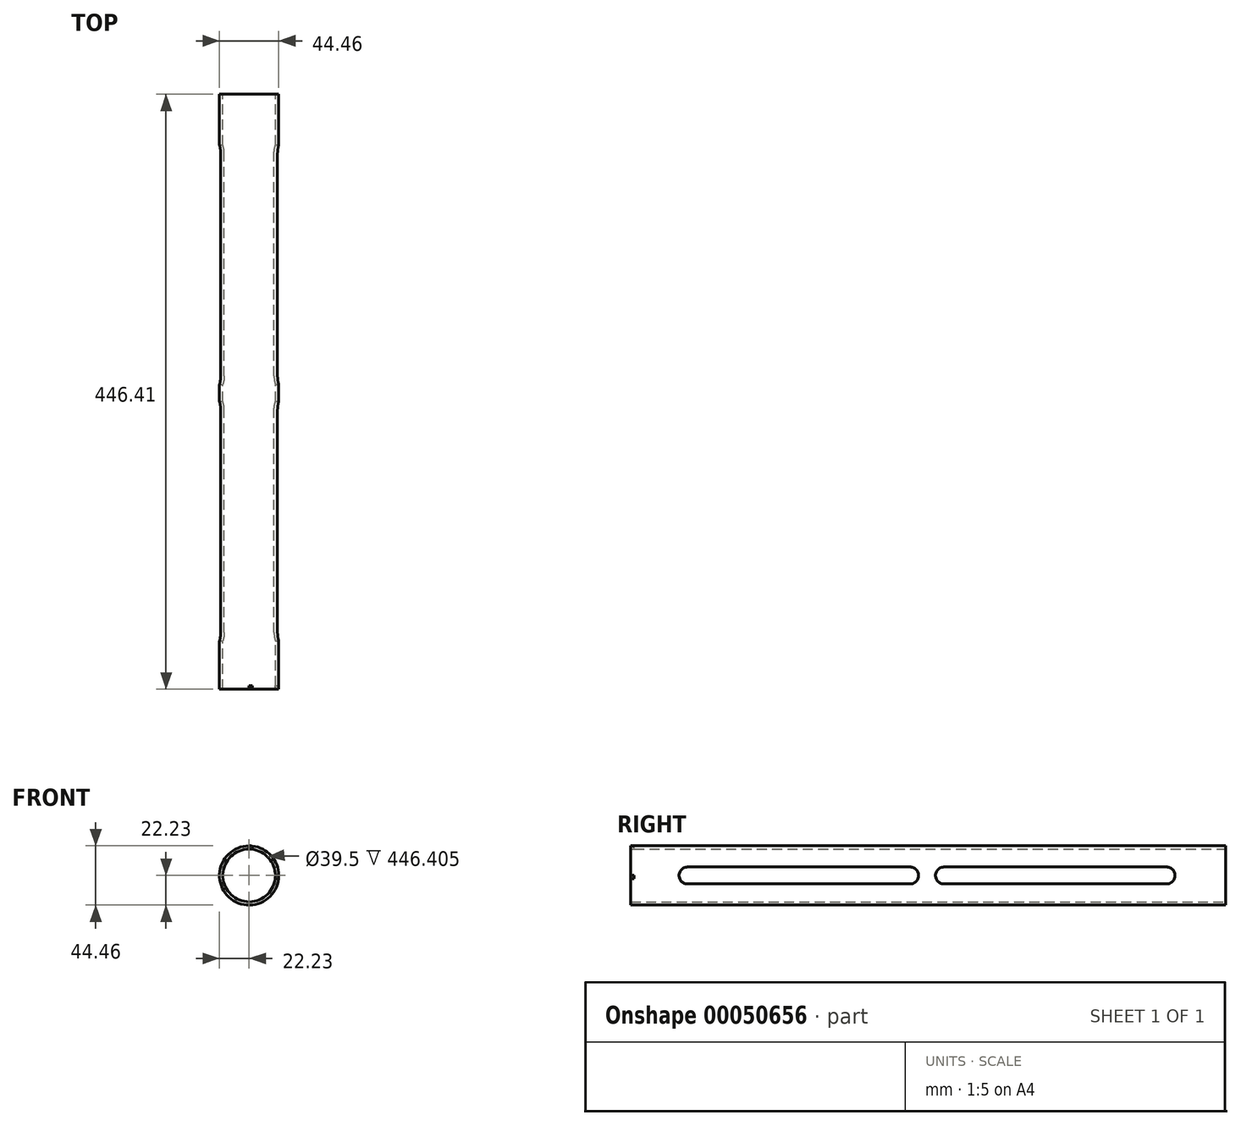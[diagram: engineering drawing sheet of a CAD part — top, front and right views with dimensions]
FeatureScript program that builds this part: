
annotation { "Feature Type Name" : "Feature", "Feature Type Description" : "" }
export const myFeature = defineFeature(function(context is Context, id is Id, definition is map)
    precondition{}
    {
        {
            var Q0;
            Q0=qCreatedBy(makeId("Front.planeOp"),FACE);
            var sketch = newSketch(context, id + "F0", { "sketchPlane" : qUnion([Q0])});
            skCircle(sketch, "E0", {"center": v(0, 0) * mm, "radius": 22.23 * mm});
            skCircle(sketch, "E1", {"center": v(0, 0) * mm, "radius": 19.75 * mm});
            skSolve(sketch);
        }
        {
            var Q0;
            Q0 = qSketchRegion(id + "F0", true);
            extrude(context, id + "F1", {"entities" : qUnion([Q0]), "depth" : 446.4 * mm});
        }
        {
            var Q0;
            Q0=qCreatedBy(makeId("Right.planeOp"),FACE);
            var sketch = newSketch(context, id + "F2", { "sketchPlane" : qUnion([Q0])});
            skLineSegment(sketch, "E2.bottom", {"start": v(-38.1, 0) * mm, "end": v(-155.7, 0) * mm});
            skLineSegment(sketch, "E2.top", {"start": v(-44.45, 6.35) * mm, "end": v(-211.46, 6.35) * mm});
            skLineSegment(sketch, "E2.left", {"start": v(-38.1, 0) * mm, "end": v(-38.1, 0) * mm});
            skPoint(sketch, "E3.visualSharp", {"position": v(-152.9, 6.35) * mm});
            skArc(sketch, "E3.filletArc", {"start": v(-211.46, 6.35) * mm, "mid": v(-215.95, 4.5) * mm, "end": v(-217.8, 0) * mm});
            skPoint(sketch, "E4.visualSharp", {"position": v(-38.1, 6.35) * mm});
            skArc(sketch, "E4.filletArc", {"start": v(-38.1, 0) * mm, "mid": v(-39.96, 4.5) * mm, "end": v(-44.45, 6.35) * mm});
            skArc(sketch, "E5.MirrorCS", {"start": v(-211.46, -6.35) * mm, "mid": v(-215.95, -4.5) * mm, "end": v(-217.8, 0) * mm});
            skPoint(sketch, "E6.MirrorP", {"position": v(-38.1, -6.35) * mm});
            skLineSegment(sketch, "E7.MirrorCS", {"start": v(-44.45, -6.35) * mm, "end": v(-211.46, -6.35) * mm});
            skArc(sketch, "E8.MirrorCS", {"start": v(-38.1, 0) * mm, "mid": v(-39.96, -4.5) * mm, "end": v(-44.45, -6.35) * mm});
            skPoint(sketch, "E9.MirrorP", {"position": v(-152.9, -6.35) * mm});
            skLineSegment(sketch, "E10", {"start": v(-224.16, 31.09) * mm, "end": v(-224.16, -31.58) * mm, "construction": true});
            skLineSegment(sketch, "E11.MirrorCS", {"start": v(-410.21, 0) * mm, "end": v(-410.21, 0) * mm});
            skLineSegment(sketch, "E12.MirrorCS", {"start": v(-403.86, 6.35) * mm, "end": v(-236.86, 6.35) * mm});
            skLineSegment(sketch, "E13.MirrorCS", {"start": v(-403.86, -6.35) * mm, "end": v(-236.86, -6.35) * mm});
            skArc(sketch, "E14.MirrorCS", {"start": v(-236.86, -6.35) * mm, "mid": v(-232.36, -4.5) * mm, "end": v(-230.5, 0) * mm});
            skArc(sketch, "E15.MirrorCS", {"start": v(-410.21, 0) * mm, "mid": v(-408.35, 4.5) * mm, "end": v(-403.86, 6.35) * mm});
            skArc(sketch, "E16.MirrorCS", {"start": v(-236.86, 6.35) * mm, "mid": v(-232.36, 4.5) * mm, "end": v(-230.5, 0) * mm});
            skPoint(sketch, "E17.MirrorP", {"position": v(-410.21, 6.35) * mm});
            skPoint(sketch, "E18.MirrorP", {"position": v(-410.21, -6.35) * mm});
            skArc(sketch, "E19.MirrorCS", {"start": v(-410.21, 0) * mm, "mid": v(-408.35, -4.5) * mm, "end": v(-403.86, -6.35) * mm});
            skSolve(sketch);
        }
        {
            var Q0;
            Q0 = qSketchRegion(id + "F2", true);
            extrude(context, id + "F3", {"entities" : qUnion([Q0]), "operationType" : NewBodyOperationType.REMOVE, "endBound" : BoundingType.SYMMETRIC, "oppositeDirection" : true, "depth" : 127 * mm});
        }
        {
            var Q0;
            Q0=makeQuery(id+"F1.opExtrude","CAP_FACE",FACE,{"disambiguationData":[OSD([sQuery(id+"F0.wireOp",EDGE,"E0"),sQuery(id+"F0.wireOp",EDGE,"E1")])],"isStart":false});
            var sketch = newSketch(context, id + "F4", { "sketchPlane" : qUnion([Q0])});
            skLineSegment(sketch, "E20.bottom", {"start": v(18.96, 0) * mm, "end": v(26.86, 0) * mm});
            skLineSegment(sketch, "E20.top", {"start": v(18.96, -2.54) * mm, "end": v(26.86, -2.54) * mm});
            skLineSegment(sketch, "E20.left", {"start": v(18.96, 0) * mm, "end": v(18.96, -2.54) * mm});
            skLineSegment(sketch, "E20.right", {"start": v(26.86, 0) * mm, "end": v(26.86, -2.54) * mm});
            skLineSegment(sketch, "E21.bottom", {"start": v(0, 19.66) * mm, "end": v(2.54, 19.66) * mm});
            skLineSegment(sketch, "E21.top", {"start": v(0, 28.48) * mm, "end": v(2.54, 28.48) * mm});
            skLineSegment(sketch, "E21.left", {"start": v(0, 19.66) * mm, "end": v(0, 28.48) * mm});
            skLineSegment(sketch, "E21.right", {"start": v(2.54, 19.66) * mm, "end": v(2.54, 28.48) * mm});
            skSolve(sketch);
        }
        {
            var Q0;
            Q0 = qSketchRegion(id + "F4", true);
            extrude(context, id + "F5", {"entities" : qUnion([Q0]), "operationType" : NewBodyOperationType.REMOVE, "oppositeDirection" : true, "depth" : 2.54 * mm});
        }
    });
